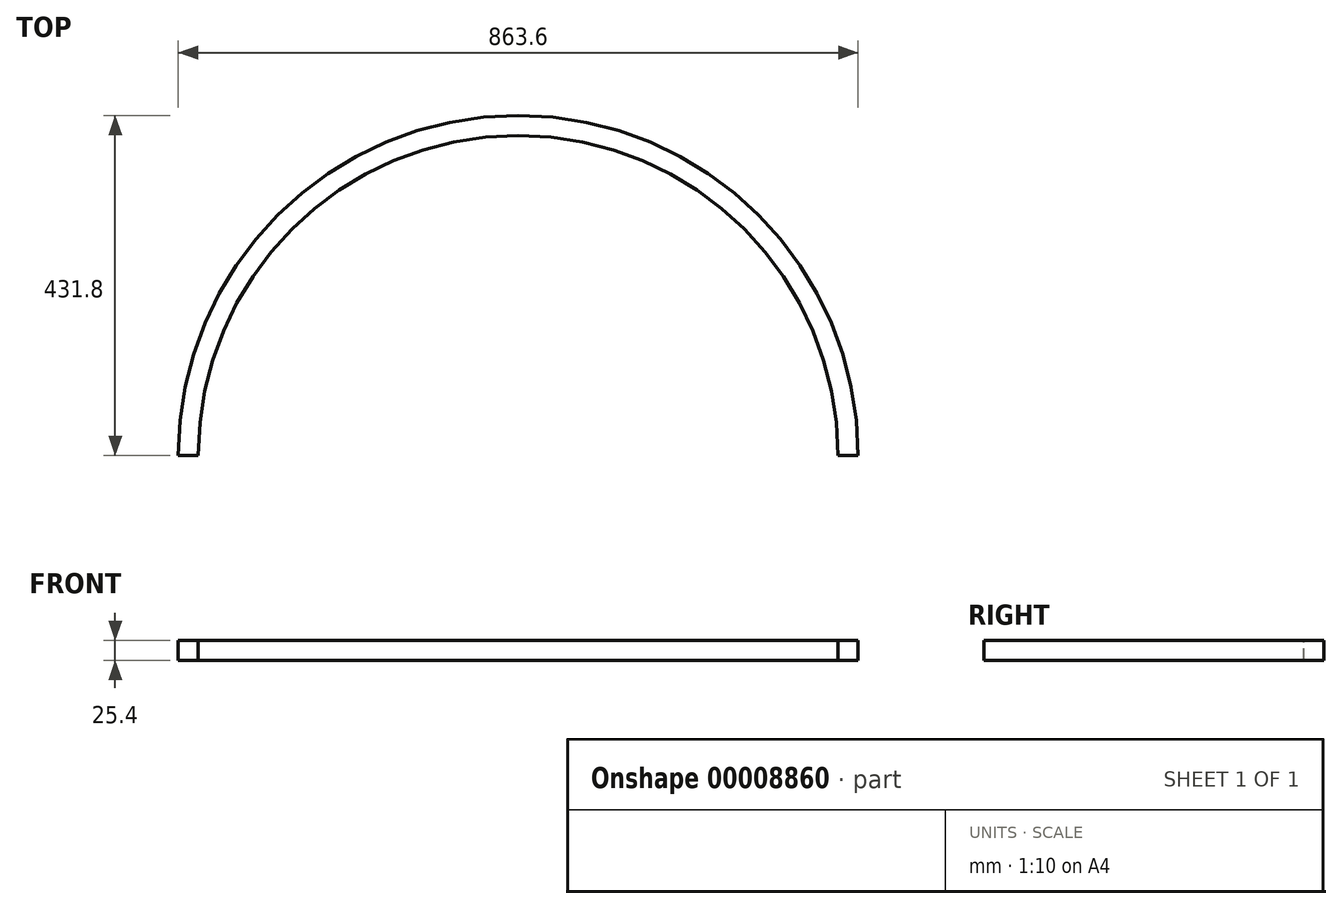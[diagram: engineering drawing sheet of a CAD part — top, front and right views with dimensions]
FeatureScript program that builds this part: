
annotation { "Feature Type Name" : "Feature", "Feature Type Description" : "" }
export const myFeature = defineFeature(function(context is Context, id is Id, definition is map)
    precondition{}
    {
        {
            var Q0;
            Q0=qCreatedBy(makeId("Front.planeOp"),FACE);
            var sketch = newSketch(context, id + "F0", { "sketchPlane" : qUnion([Q0])});
            skLineSegment(sketch, "E0.bottom", {"start": v(-13.04, 10.83) * mm, "end": v(12.36, 10.83) * mm});
            skLineSegment(sketch, "E0.top", {"start": v(-13.04, -14.57) * mm, "end": v(12.36, -14.57) * mm});
            skLineSegment(sketch, "E0.left", {"start": v(-13.04, 10.83) * mm, "end": v(-13.04, -14.57) * mm});
            skLineSegment(sketch, "E0.right", {"start": v(12.36, 10.83) * mm, "end": v(12.36, -14.57) * mm});
            skLineSegment(sketch, "E1", {"start": v(418.76, 19.21) * mm, "end": v(418.76, -34.27) * mm, "construction": true});
            skSolve(sketch);
        }
        {
            var Q0;
            Q0=makeQuery(id+"F0.imprint","IMPRINT",FACE,{"disambiguationData":[TD([[makeQuery(id+"F0.imprint","IMPRINT",EDGE,{"derivedFrom":sQuery(id+"F0.wireOp",EDGE,"E0.bottom")}),-1.0]])]});
            var Q1;
            Q1=sQuery(id+"F0.wireOp",EDGE,"E1");
            revolve(context, id + "F1", {"entities" : qUnion([Q0]), "axis" : qUnion([Q1]), "revolveType" : RevolveType.ONE_DIRECTION, "angle" : 180 * degree});
        }
    });
